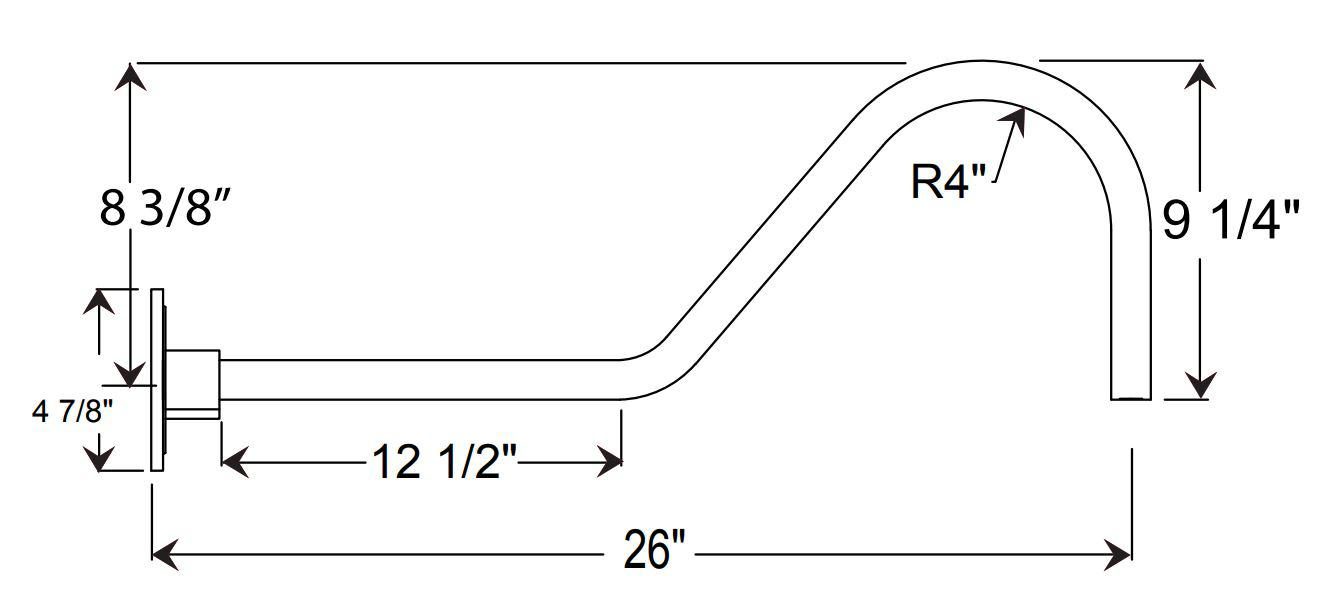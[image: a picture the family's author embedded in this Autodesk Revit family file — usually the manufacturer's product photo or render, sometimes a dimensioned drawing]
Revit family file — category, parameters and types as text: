
# Revit family: Willow 16,20,24,30 LED
name_source: partatom
category: Lighting Fixtures
units: mm (PartAtom-declared; Revit-internal decimal feet)

## family parameters
Always vertical = Yes
Cut with Voids When Loaded = No
Light Source = Yes
OmniClass Number = 23.80.70.00
OmniClass Title = Lighting
Part Type = Normal
Room Calculation Point = No
Round Connector Dimension = Use Diameter
Shared = No
Work Plane-Based = No

## types (4) — shared parameters
Body Colour = Spun aluminium
Body Material = body
CRI = >90
Color Filter = 16777215
Construction Material = Heavy Duty spun aluminum.
Default Elevation = 0' - 0"
Description = 120-277 Voltage
Dimming = 1%
Dimming Lamp Color Temperature Shift = <None>
Efficiency = 65-125 lumens per watt
Fixture Finish = Fixture Finish
GLASS = Glass
Lamp = LED
Life = L70 50,000 hours
Load Classification = Lighting
Manufacturer = ANP Lighting
Power Factor = 1
Tilt Angle = 90.00°
URL = https://www.anplighting.com
Voltage = 277 V
Warranty = 5 year limited warranty

## per-type parameters (varying)
| type | Apparent Load | Fixture Diameter | Fixture Height | MDW16 | MDW20 | MDW24 | MDW30 | Photometric Web File | Wattage Comments | Weight |
| MDW16 | 16 VA | 1' - 4" | 0' - 4 1/2" | Yes | No | No | No | MDW16M016LD35K.IES | 16W | 5 lbs |
| MDW20 | 16 VA | 1' - 8" | 0' - 5 1/2" | No | Yes | No | No | MDW16M016LD35K.IES | 16W | 5.5 lbs |
| MDW24 | 24 VA | 2' - 0" | 0' - 6 1/2" | No | No | Yes | No | MDW24M024LD35K.IES | 24W | 6.0 lbs |
| MDW30 | 24 VA | 2' - 6" | 0' - 8 1/2" | No | No | No | Yes | MDO24M024LD35K.IES | 24W | 6.5 lbs |

note: column(s) folded — value = type name in every type: Model

## geometry (parser evidence)
native form markers: Sweep x22
no freeform markers — native parametric forms only
